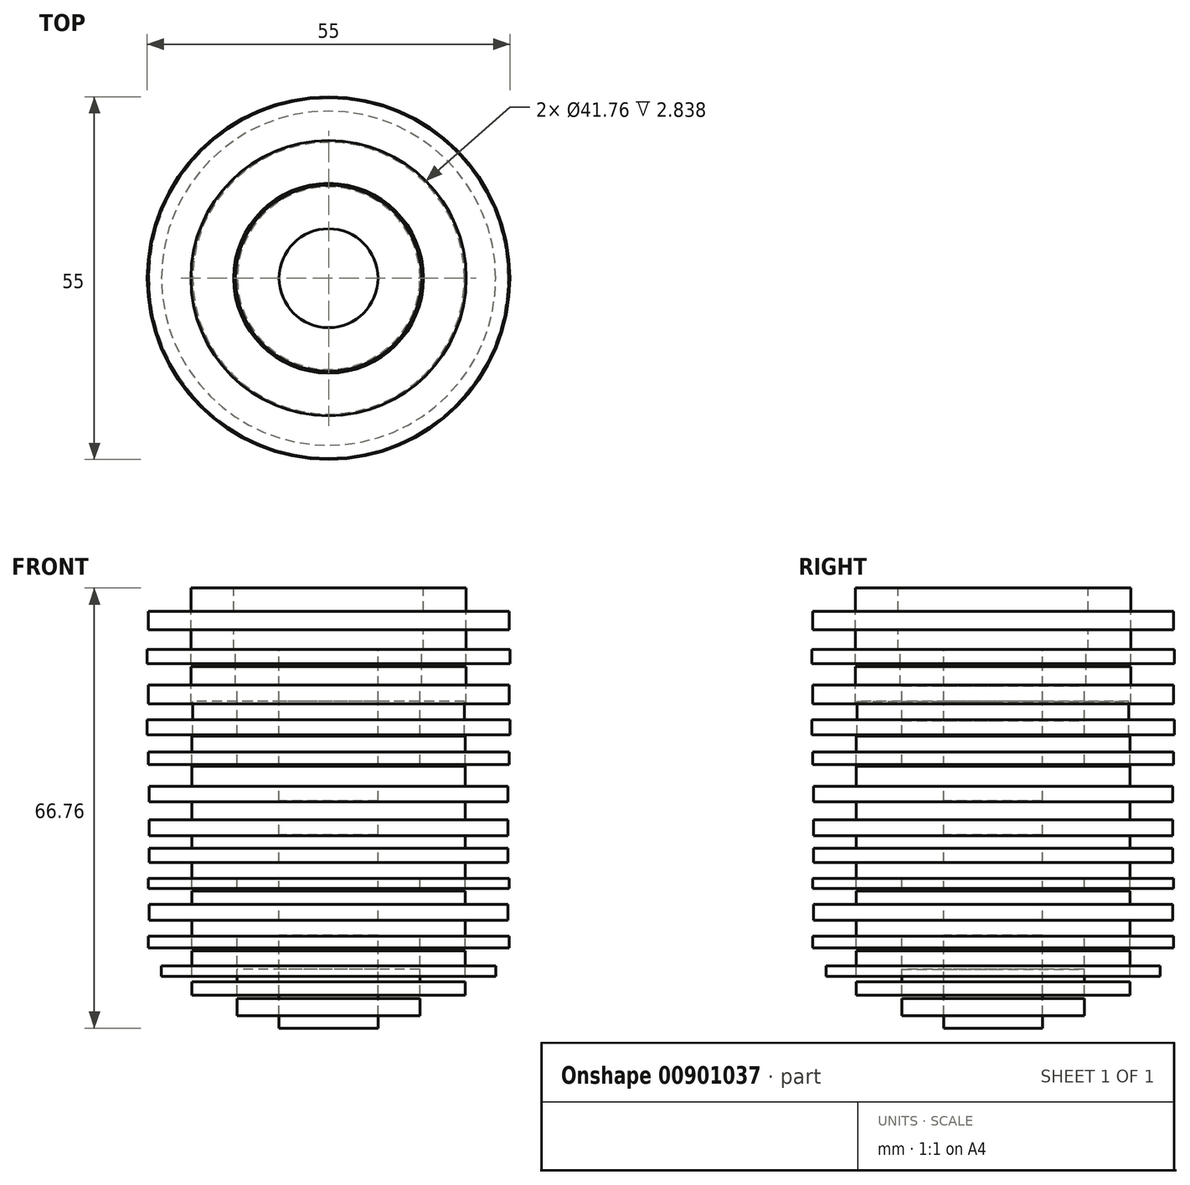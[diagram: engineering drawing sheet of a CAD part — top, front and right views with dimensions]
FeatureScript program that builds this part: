
annotation { "Feature Type Name" : "Feature", "Feature Type Description" : "" }
export const myFeature = defineFeature(function(context is Context, id is Id, definition is map)
    precondition{}
    {
        {
            var Q0;
            Q0=qCreatedBy(makeId("Front.planeOp"),FACE);
            var sketch = newSketch(context, id + "F0", { "sketchPlane" : qUnion([Q0])});
            skArc(sketch, "E0", {"start": v(0, -38.1) * mm, "mid": v(38.1, 0) * mm, "end": v(0, 38.1) * mm});
            skLineSegment(sketch, "E1", {"start": v(0, 38.1) * mm, "end": v(0, -38.1) * mm});
            skSolve(sketch);
        }
        {
            var Q0;
            Q0=qCreatedBy(makeId("Front.planeOp"),FACE);
            var sketch = newSketch(context, id + "F1", { "sketchPlane" : qUnion([Q0])});
            skLineSegment(sketch, "E2.bottom", {"start": v(7.5, 20.75) * mm, "end": v(14.12, 20.75) * mm});
            skLineSegment(sketch, "E2.top", {"start": v(7.5, 18.18) * mm, "end": v(14.12, 18.18) * mm});
            skLineSegment(sketch, "E2.left", {"start": v(7.5, 20.75) * mm, "end": v(7.5, 18.18) * mm});
            skLineSegment(sketch, "E2.right", {"start": v(14.12, 20.75) * mm, "end": v(14.12, 18.18) * mm});
            skLineSegment(sketch, "E3.bottom", {"start": v(7.5, 18.18) * mm, "end": v(0, 18.18) * mm});
            skLineSegment(sketch, "E3.top", {"start": v(7.5, 15.2) * mm, "end": v(0, 15.2) * mm});
            skLineSegment(sketch, "E3.left", {"start": v(7.5, 18.18) * mm, "end": v(7.5, 15.2) * mm});
            skLineSegment(sketch, "E3.right", {"start": v(0, 18.18) * mm, "end": v(0, 15.2) * mm});
            skLineSegment(sketch, "E4.bottom", {"start": v(7.5, 15.2) * mm, "end": v(13.85, 15.2) * mm});
            skLineSegment(sketch, "E4.top", {"start": v(7.5, 12.9) * mm, "end": v(13.85, 12.9) * mm});
            skLineSegment(sketch, "E4.left", {"start": v(7.5, 15.2) * mm, "end": v(7.5, 12.9) * mm});
            skLineSegment(sketch, "E4.right", {"start": v(13.85, 15.2) * mm, "end": v(13.85, 12.9) * mm});
            skLineSegment(sketch, "E5.bottom", {"start": v(7.5, 12.9) * mm, "end": v(0, 12.9) * mm});
            skLineSegment(sketch, "E5.top", {"start": v(7.5, 9.93) * mm, "end": v(0, 9.93) * mm});
            skLineSegment(sketch, "E5.left", {"start": v(7.5, 12.9) * mm, "end": v(7.5, 9.93) * mm});
            skLineSegment(sketch, "E5.right", {"start": v(0, 12.9) * mm, "end": v(0, 9.93) * mm});
            skLineSegment(sketch, "E6.bottom", {"start": v(7.5, 9.93) * mm, "end": v(13.85, 9.93) * mm});
            skLineSegment(sketch, "E6.top", {"start": v(7.5, 7.64) * mm, "end": v(13.85, 7.64) * mm});
            skLineSegment(sketch, "E6.left", {"start": v(7.5, 9.93) * mm, "end": v(7.5, 7.64) * mm});
            skLineSegment(sketch, "E6.right", {"start": v(13.85, 9.93) * mm, "end": v(13.85, 7.64) * mm});
            skLineSegment(sketch, "E7.bottom", {"start": v(7.5, 7.64) * mm, "end": v(0, 7.64) * mm});
            skLineSegment(sketch, "E7.top", {"start": v(7.5, 5.2) * mm, "end": v(0, 5.2) * mm});
            skLineSegment(sketch, "E7.left", {"start": v(7.5, 7.64) * mm, "end": v(7.5, 5.2) * mm});
            skLineSegment(sketch, "E7.right", {"start": v(0, 7.64) * mm, "end": v(0, 5.2) * mm});
            skLineSegment(sketch, "E8.bottom", {"start": v(7.5, 5.2) * mm, "end": v(13.85, 5.2) * mm});
            skLineSegment(sketch, "E8.top", {"start": v(7.5, 3.04) * mm, "end": v(13.85, 3.04) * mm});
            skLineSegment(sketch, "E8.left", {"start": v(7.5, 5.2) * mm, "end": v(7.5, 3.04) * mm});
            skLineSegment(sketch, "E8.right", {"start": v(13.85, 5.2) * mm, "end": v(13.85, 3.04) * mm});
            skLineSegment(sketch, "E9.bottom", {"start": v(7.5, 3.04) * mm, "end": v(0, 3.04) * mm});
            skLineSegment(sketch, "E9.top", {"start": v(7.5, 0) * mm, "end": v(0, 0) * mm});
            skLineSegment(sketch, "E9.left", {"start": v(7.5, 3.04) * mm, "end": v(7.5, 0) * mm});
            skLineSegment(sketch, "E9.right", {"start": v(0, 3.04) * mm, "end": v(0, 0) * mm});
            skLineSegment(sketch, "E10.bottom", {"start": v(7.5, 0) * mm, "end": v(13.85, 0) * mm});
            skLineSegment(sketch, "E10.top", {"start": v(7.5, -2.23) * mm, "end": v(13.85, -2.23) * mm});
            skLineSegment(sketch, "E10.left", {"start": v(7.5, 0) * mm, "end": v(7.5, -2.23) * mm});
            skLineSegment(sketch, "E10.right", {"start": v(13.85, 0) * mm, "end": v(13.85, -2.23) * mm});
            skLineSegment(sketch, "E11.bottom", {"start": v(7.5, -2.23) * mm, "end": v(0, -2.23) * mm});
            skLineSegment(sketch, "E11.top", {"start": v(7.5, -5.07) * mm, "end": v(0, -5.07) * mm});
            skLineSegment(sketch, "E11.left", {"start": v(7.5, -2.23) * mm, "end": v(7.5, -5.07) * mm});
            skLineSegment(sketch, "E11.right", {"start": v(0, -2.23) * mm, "end": v(0, -5.07) * mm});
            skLineSegment(sketch, "E12.bottom", {"start": v(7.5, -5.07) * mm, "end": v(13.85, -5.07) * mm});
            skLineSegment(sketch, "E12.top", {"start": v(7.5, -7.37) * mm, "end": v(13.85, -7.37) * mm});
            skLineSegment(sketch, "E12.left", {"start": v(7.5, -5.07) * mm, "end": v(7.5, -7.37) * mm});
            skLineSegment(sketch, "E12.right", {"start": v(13.85, -5.07) * mm, "end": v(13.85, -7.37) * mm});
            skLineSegment(sketch, "E13.bottom", {"start": v(7.5, -7.37) * mm, "end": v(0, -7.37) * mm});
            skLineSegment(sketch, "E13.top", {"start": v(7.5, -9.4) * mm, "end": v(0, -9.4) * mm});
            skLineSegment(sketch, "E13.left", {"start": v(7.5, -7.37) * mm, "end": v(7.5, -9.4) * mm});
            skLineSegment(sketch, "E13.right", {"start": v(0, -7.37) * mm, "end": v(0, -9.4) * mm});
            skLineSegment(sketch, "E14.bottom", {"start": v(7.5, -9.4) * mm, "end": v(13.85, -9.4) * mm});
            skLineSegment(sketch, "E14.top", {"start": v(7.5, -11.56) * mm, "end": v(13.85, -11.56) * mm});
            skLineSegment(sketch, "E14.left", {"start": v(7.5, -9.4) * mm, "end": v(7.5, -11.56) * mm});
            skLineSegment(sketch, "E14.right", {"start": v(13.85, -9.4) * mm, "end": v(13.85, -11.56) * mm});
            skLineSegment(sketch, "E15.bottom", {"start": v(7.5, -11.56) * mm, "end": v(0, -11.56) * mm});
            skLineSegment(sketch, "E15.top", {"start": v(7.5, -13.99) * mm, "end": v(0, -13.99) * mm});
            skLineSegment(sketch, "E15.left", {"start": v(7.5, -11.56) * mm, "end": v(7.5, -13.99) * mm});
            skLineSegment(sketch, "E15.right", {"start": v(0, -11.56) * mm, "end": v(0, -13.99) * mm});
            skLineSegment(sketch, "E16.bottom", {"start": v(7.5, -13.99) * mm, "end": v(13.85, -13.99) * mm});
            skLineSegment(sketch, "E16.top", {"start": v(7.5, -15.88) * mm, "end": v(13.85, -15.88) * mm});
            skLineSegment(sketch, "E16.left", {"start": v(7.5, -13.99) * mm, "end": v(7.5, -15.88) * mm});
            skLineSegment(sketch, "E16.right", {"start": v(13.85, -13.99) * mm, "end": v(13.85, -15.88) * mm});
            skLineSegment(sketch, "E17.bottom", {"start": v(7.5, -15.88) * mm, "end": v(0, -15.88) * mm});
            skLineSegment(sketch, "E17.top", {"start": v(7.5, -17.9) * mm, "end": v(0, -17.9) * mm});
            skLineSegment(sketch, "E17.left", {"start": v(7.5, -15.88) * mm, "end": v(7.5, -17.9) * mm});
            skLineSegment(sketch, "E17.right", {"start": v(0, -15.88) * mm, "end": v(0, -17.9) * mm});
            skLineSegment(sketch, "E18.bottom", {"start": v(7.5, -17.9) * mm, "end": v(13.85, -17.9) * mm});
            skLineSegment(sketch, "E18.top", {"start": v(7.5, -20.34) * mm, "end": v(13.85, -20.34) * mm});
            skLineSegment(sketch, "E18.left", {"start": v(7.5, -17.9) * mm, "end": v(7.5, -20.34) * mm});
            skLineSegment(sketch, "E18.right", {"start": v(13.85, -17.9) * mm, "end": v(13.85, -20.34) * mm});
            skLineSegment(sketch, "E19.bottom", {"start": v(7.5, -20.34) * mm, "end": v(0, -20.34) * mm});
            skLineSegment(sketch, "E19.top", {"start": v(7.5, -22.64) * mm, "end": v(0, -22.64) * mm});
            skLineSegment(sketch, "E19.left", {"start": v(7.5, -20.34) * mm, "end": v(7.5, -22.64) * mm});
            skLineSegment(sketch, "E19.right", {"start": v(0, -20.34) * mm, "end": v(0, -22.64) * mm});
            skLineSegment(sketch, "E20.bottom", {"start": v(7.5, -22.64) * mm, "end": v(13.85, -22.64) * mm});
            skLineSegment(sketch, "E20.top", {"start": v(7.5, -24.94) * mm, "end": v(13.85, -24.94) * mm});
            skLineSegment(sketch, "E20.left", {"start": v(7.5, -22.64) * mm, "end": v(7.5, -24.94) * mm});
            skLineSegment(sketch, "E20.right", {"start": v(13.85, -22.64) * mm, "end": v(13.85, -24.94) * mm});
            skLineSegment(sketch, "E21.bottom", {"start": v(7.5, -24.94) * mm, "end": v(0, -24.94) * mm});
            skLineSegment(sketch, "E21.top", {"start": v(7.5, -27.77) * mm, "end": v(0, -27.77) * mm});
            skLineSegment(sketch, "E21.left", {"start": v(7.5, -24.94) * mm, "end": v(7.5, -27.77) * mm});
            skLineSegment(sketch, "E21.right", {"start": v(0, -24.94) * mm, "end": v(0, -27.77) * mm});
            skLineSegment(sketch, "E22.bottom", {"start": v(7.5, -27.77) * mm, "end": v(13.85, -27.77) * mm});
            skLineSegment(sketch, "E22.top", {"start": v(7.5, -29.67) * mm, "end": v(13.85, -29.67) * mm});
            skLineSegment(sketch, "E22.left", {"start": v(7.5, -27.77) * mm, "end": v(7.5, -29.67) * mm});
            skLineSegment(sketch, "E22.right", {"start": v(13.85, -27.77) * mm, "end": v(13.85, -29.67) * mm});
            skLineSegment(sketch, "E23.bottom", {"start": v(7.5, -29.67) * mm, "end": v(0, -29.67) * mm});
            skLineSegment(sketch, "E23.top", {"start": v(7.5, -32.23) * mm, "end": v(0, -32.23) * mm});
            skLineSegment(sketch, "E23.left", {"start": v(7.5, -29.67) * mm, "end": v(7.5, -32.23) * mm});
            skLineSegment(sketch, "E23.right", {"start": v(0, -29.67) * mm, "end": v(0, -32.23) * mm});
            skLineSegment(sketch, "E24.bottom", {"start": v(7.5, -32.23) * mm, "end": v(13.85, -32.23) * mm});
            skLineSegment(sketch, "E24.top", {"start": v(7.5, -34.8) * mm, "end": v(13.85, -34.8) * mm});
            skLineSegment(sketch, "E24.left", {"start": v(7.5, -32.23) * mm, "end": v(7.5, -34.8) * mm});
            skLineSegment(sketch, "E24.right", {"start": v(13.85, -32.23) * mm, "end": v(13.85, -34.8) * mm});
            skLineSegment(sketch, "E25.bottom", {"start": v(7.5, -34.8) * mm, "end": v(0, -34.8) * mm});
            skLineSegment(sketch, "E25.top", {"start": v(7.5, -36.7) * mm, "end": v(0, -36.7) * mm});
            skLineSegment(sketch, "E25.left", {"start": v(7.5, -34.8) * mm, "end": v(7.5, -36.7) * mm});
            skLineSegment(sketch, "E25.right", {"start": v(0, -34.8) * mm, "end": v(0, -36.7) * mm});
            skLineSegment(sketch, "E26.bottom", {"start": v(14.4, 30.07) * mm, "end": v(20.88, 30.07) * mm});
            skLineSegment(sketch, "E26.top", {"start": v(14.4, 26.56) * mm, "end": v(20.88, 26.56) * mm});
            skLineSegment(sketch, "E26.left", {"start": v(14.4, 30.07) * mm, "end": v(14.4, 26.56) * mm});
            skLineSegment(sketch, "E26.right", {"start": v(20.88, 30.07) * mm, "end": v(20.88, 26.56) * mm});
            skLineSegment(sketch, "E27.bottom", {"start": v(14.4, 23.72) * mm, "end": v(20.88, 23.72) * mm});
            skLineSegment(sketch, "E27.top", {"start": v(14.4, 20.75) * mm, "end": v(20.88, 20.75) * mm});
            skLineSegment(sketch, "E27.left", {"start": v(14.4, 23.72) * mm, "end": v(14.4, 20.75) * mm});
            skLineSegment(sketch, "E27.right", {"start": v(20.88, 23.72) * mm, "end": v(20.88, 20.75) * mm});
            skLineSegment(sketch, "E28.bottom", {"start": v(14.12, 18.18) * mm, "end": v(20.88, 18.18) * mm});
            skLineSegment(sketch, "E28.top", {"start": v(14.12, 15.34) * mm, "end": v(20.88, 15.34) * mm});
            skLineSegment(sketch, "E28.left", {"start": v(14.12, 18.18) * mm, "end": v(14.12, 15.34) * mm});
            skLineSegment(sketch, "E28.right", {"start": v(20.88, 18.18) * mm, "end": v(20.88, 15.34) * mm});
            skLineSegment(sketch, "E29.bottom", {"start": v(13.85, 12.9) * mm, "end": v(20.61, 12.9) * mm});
            skLineSegment(sketch, "E29.top", {"start": v(13.85, 10.07) * mm, "end": v(20.61, 10.07) * mm});
            skLineSegment(sketch, "E29.left", {"start": v(13.85, 12.9) * mm, "end": v(13.85, 10.07) * mm});
            skLineSegment(sketch, "E29.right", {"start": v(20.61, 12.9) * mm, "end": v(20.61, 10.07) * mm});
            skLineSegment(sketch, "E30.bottom", {"start": v(13.85, 7.64) * mm, "end": v(20.75, 7.64) * mm});
            skLineSegment(sketch, "E30.top", {"start": v(13.85, 5.2) * mm, "end": v(20.75, 5.2) * mm});
            skLineSegment(sketch, "E30.left", {"start": v(13.85, 7.64) * mm, "end": v(13.85, 5.2) * mm});
            skLineSegment(sketch, "E30.right", {"start": v(20.75, 7.64) * mm, "end": v(20.75, 5.2) * mm});
            skLineSegment(sketch, "E31.bottom", {"start": v(13.85, 3.04) * mm, "end": v(20.75, 3.04) * mm});
            skLineSegment(sketch, "E31.top", {"start": v(13.85, 0) * mm, "end": v(20.75, 0) * mm});
            skLineSegment(sketch, "E31.left", {"start": v(13.85, 3.04) * mm, "end": v(13.85, 0) * mm});
            skLineSegment(sketch, "E31.right", {"start": v(20.75, 3.04) * mm, "end": v(20.75, 0) * mm});
            skLineSegment(sketch, "E32.bottom", {"start": v(13.85, -2.23) * mm, "end": v(20.75, -2.23) * mm});
            skLineSegment(sketch, "E32.top", {"start": v(13.85, -5.07) * mm, "end": v(20.75, -5.07) * mm});
            skLineSegment(sketch, "E32.left", {"start": v(13.85, -2.23) * mm, "end": v(13.85, -5.07) * mm});
            skLineSegment(sketch, "E32.right", {"start": v(20.75, -2.23) * mm, "end": v(20.75, -5.07) * mm});
            skLineSegment(sketch, "E33.bottom", {"start": v(13.85, -7.37) * mm, "end": v(20.75, -7.37) * mm});
            skLineSegment(sketch, "E33.top", {"start": v(13.85, -9.4) * mm, "end": v(20.75, -9.4) * mm});
            skLineSegment(sketch, "E33.left", {"start": v(13.85, -7.37) * mm, "end": v(13.85, -9.4) * mm});
            skLineSegment(sketch, "E33.right", {"start": v(20.75, -7.37) * mm, "end": v(20.75, -9.4) * mm});
            skLineSegment(sketch, "E34.bottom", {"start": v(13.85, -11.56) * mm, "end": v(20.75, -11.56) * mm});
            skLineSegment(sketch, "E34.top", {"start": v(13.85, -13.99) * mm, "end": v(20.75, -13.99) * mm});
            skLineSegment(sketch, "E34.left", {"start": v(13.85, -11.56) * mm, "end": v(13.85, -13.99) * mm});
            skLineSegment(sketch, "E34.right", {"start": v(20.75, -11.56) * mm, "end": v(20.75, -13.99) * mm});
            skLineSegment(sketch, "E35.bottom", {"start": v(13.85, -15.88) * mm, "end": v(20.75, -15.88) * mm});
            skLineSegment(sketch, "E35.top", {"start": v(13.85, -17.9) * mm, "end": v(20.75, -17.9) * mm});
            skLineSegment(sketch, "E35.left", {"start": v(13.85, -15.88) * mm, "end": v(13.85, -17.9) * mm});
            skLineSegment(sketch, "E35.right", {"start": v(20.75, -15.88) * mm, "end": v(20.75, -17.9) * mm});
            skLineSegment(sketch, "E36.bottom", {"start": v(13.85, -20.34) * mm, "end": v(20.75, -20.34) * mm});
            skLineSegment(sketch, "E36.top", {"start": v(13.85, -22.77) * mm, "end": v(20.75, -22.77) * mm});
            skLineSegment(sketch, "E36.left", {"start": v(13.85, -20.34) * mm, "end": v(13.85, -22.77) * mm});
            skLineSegment(sketch, "E36.right", {"start": v(20.75, -20.34) * mm, "end": v(20.75, -22.77) * mm});
            skLineSegment(sketch, "E37.bottom", {"start": v(13.85, -24.94) * mm, "end": v(20.75, -24.94) * mm});
            skLineSegment(sketch, "E37.top", {"start": v(13.85, -27.23) * mm, "end": v(20.75, -27.23) * mm});
            skLineSegment(sketch, "E37.left", {"start": v(13.85, -24.94) * mm, "end": v(13.85, -27.23) * mm});
            skLineSegment(sketch, "E37.right", {"start": v(20.75, -24.94) * mm, "end": v(20.75, -27.23) * mm});
            skLineSegment(sketch, "E38.bottom", {"start": v(13.85, -29.67) * mm, "end": v(20.75, -29.67) * mm});
            skLineSegment(sketch, "E38.top", {"start": v(13.85, -31.7) * mm, "end": v(20.75, -31.7) * mm});
            skLineSegment(sketch, "E38.left", {"start": v(13.85, -29.67) * mm, "end": v(13.85, -31.7) * mm});
            skLineSegment(sketch, "E38.right", {"start": v(20.75, -29.67) * mm, "end": v(20.75, -31.7) * mm});
            skLineSegment(sketch, "E39.bottom", {"start": v(20.88, 26.56) * mm, "end": v(27.37, 26.56) * mm});
            skLineSegment(sketch, "E39.top", {"start": v(20.88, 23.72) * mm, "end": v(27.37, 23.72) * mm});
            skLineSegment(sketch, "E39.left", {"start": v(20.88, 26.56) * mm, "end": v(20.88, 23.72) * mm});
            skLineSegment(sketch, "E39.right", {"start": v(27.37, 26.56) * mm, "end": v(27.37, 23.72) * mm});
            skLineSegment(sketch, "E40.bottom", {"start": v(20.88, 20.75) * mm, "end": v(27.5, 20.75) * mm});
            skLineSegment(sketch, "E40.top", {"start": v(20.88, 18.58) * mm, "end": v(27.5, 18.58) * mm});
            skLineSegment(sketch, "E40.left", {"start": v(20.88, 20.75) * mm, "end": v(20.88, 18.58) * mm});
            skLineSegment(sketch, "E40.right", {"start": v(27.5, 20.75) * mm, "end": v(27.5, 18.58) * mm});
            skLineSegment(sketch, "E41.bottom", {"start": v(20.88, 15.34) * mm, "end": v(27.37, 15.34) * mm});
            skLineSegment(sketch, "E41.top", {"start": v(20.88, 12.5) * mm, "end": v(27.37, 12.5) * mm});
            skLineSegment(sketch, "E41.left", {"start": v(20.88, 15.34) * mm, "end": v(20.88, 12.5) * mm});
            skLineSegment(sketch, "E41.right", {"start": v(27.37, 15.34) * mm, "end": v(27.37, 12.5) * mm});
            skLineSegment(sketch, "E42.bottom", {"start": v(20.61, 10.07) * mm, "end": v(27.5, 10.07) * mm});
            skLineSegment(sketch, "E42.top", {"start": v(20.61, 7.77) * mm, "end": v(27.5, 7.77) * mm});
            skLineSegment(sketch, "E42.left", {"start": v(20.61, 10.07) * mm, "end": v(20.61, 7.77) * mm});
            skLineSegment(sketch, "E42.right", {"start": v(27.5, 10.07) * mm, "end": v(27.5, 7.77) * mm});
            skLineSegment(sketch, "E43.bottom", {"start": v(20.75, 5.2) * mm, "end": v(27.37, 5.2) * mm});
            skLineSegment(sketch, "E43.top", {"start": v(20.75, 3.31) * mm, "end": v(27.37, 3.31) * mm});
            skLineSegment(sketch, "E43.left", {"start": v(20.75, 5.2) * mm, "end": v(20.75, 3.31) * mm});
            skLineSegment(sketch, "E43.right", {"start": v(27.37, 5.2) * mm, "end": v(27.37, 3.31) * mm});
            skLineSegment(sketch, "E44.bottom", {"start": v(20.75, 0) * mm, "end": v(27.23, 0) * mm});
            skLineSegment(sketch, "E44.top", {"start": v(20.75, -2.37) * mm, "end": v(27.23, -2.37) * mm});
            skLineSegment(sketch, "E44.left", {"start": v(20.75, 0) * mm, "end": v(20.75, -2.37) * mm});
            skLineSegment(sketch, "E44.right", {"start": v(27.23, 0) * mm, "end": v(27.23, -2.37) * mm});
            skLineSegment(sketch, "E45.bottom", {"start": v(20.75, -5.07) * mm, "end": v(27.23, -5.07) * mm});
            skLineSegment(sketch, "E45.top", {"start": v(20.75, -7.5) * mm, "end": v(27.23, -7.5) * mm});
            skLineSegment(sketch, "E45.left", {"start": v(20.75, -5.07) * mm, "end": v(20.75, -7.5) * mm});
            skLineSegment(sketch, "E45.right", {"start": v(27.23, -5.07) * mm, "end": v(27.23, -7.5) * mm});
            skLineSegment(sketch, "E46.bottom", {"start": v(20.75, -9.4) * mm, "end": v(27.23, -9.4) * mm});
            skLineSegment(sketch, "E46.top", {"start": v(20.75, -11.56) * mm, "end": v(27.23, -11.56) * mm});
            skLineSegment(sketch, "E46.left", {"start": v(20.75, -9.4) * mm, "end": v(20.75, -11.56) * mm});
            skLineSegment(sketch, "E46.right", {"start": v(27.23, -9.4) * mm, "end": v(27.23, -11.56) * mm});
            skLineSegment(sketch, "E47.bottom", {"start": v(20.75, -13.99) * mm, "end": v(27.37, -13.99) * mm});
            skLineSegment(sketch, "E47.top", {"start": v(20.75, -15.47) * mm, "end": v(27.37, -15.47) * mm});
            skLineSegment(sketch, "E47.left", {"start": v(20.75, -13.99) * mm, "end": v(20.75, -15.47) * mm});
            skLineSegment(sketch, "E47.right", {"start": v(27.37, -13.99) * mm, "end": v(27.37, -15.47) * mm});
            skPoint(sketch, "E48.oppositeSnap0", {"position": v(17.3, -20.34) * mm});
            skLineSegment(sketch, "E48.bottom", {"start": v(20.75, -17.9) * mm, "end": v(27.23, -17.9) * mm});
            skLineSegment(sketch, "E48.top", {"start": v(20.75, -20.34) * mm, "end": v(27.23, -20.34) * mm});
            skLineSegment(sketch, "E48.left", {"start": v(20.75, -17.9) * mm, "end": v(20.75, -20.34) * mm});
            skLineSegment(sketch, "E48.right", {"start": v(27.23, -17.9) * mm, "end": v(27.23, -20.34) * mm});
            skLineSegment(sketch, "E49.bottom", {"start": v(20.75, -22.77) * mm, "end": v(27.37, -22.77) * mm});
            skLineSegment(sketch, "E49.top", {"start": v(20.75, -24.53) * mm, "end": v(27.37, -24.53) * mm});
            skLineSegment(sketch, "E49.left", {"start": v(20.75, -22.77) * mm, "end": v(20.75, -24.53) * mm});
            skLineSegment(sketch, "E49.right", {"start": v(27.37, -22.77) * mm, "end": v(27.37, -24.53) * mm});
            skLineSegment(sketch, "E50.bottom", {"start": v(20.75, -27.23) * mm, "end": v(25.34, -27.23) * mm});
            skLineSegment(sketch, "E50.top", {"start": v(20.75, -28.85) * mm, "end": v(25.34, -28.85) * mm});
            skLineSegment(sketch, "E50.left", {"start": v(20.75, -27.23) * mm, "end": v(20.75, -28.85) * mm});
            skLineSegment(sketch, "E50.right", {"start": v(25.34, -27.23) * mm, "end": v(25.34, -28.85) * mm});
            skSolve(sketch);
        }
        {
            var Q0;
            Q0 = qSketchRegion(id + "F1", true);
            var Q1;
            Q1=sQuery(id+"F0.wireOp",EDGE,"E1");
            revolve(context, id + "F2", {"surfaceOperationType" : NewSurfaceOperationType.NEW, "entities" : qUnion([Q0]), "axis" : qUnion([Q1]), "revolveType" : RevolveType.FULL});
        }
    });
